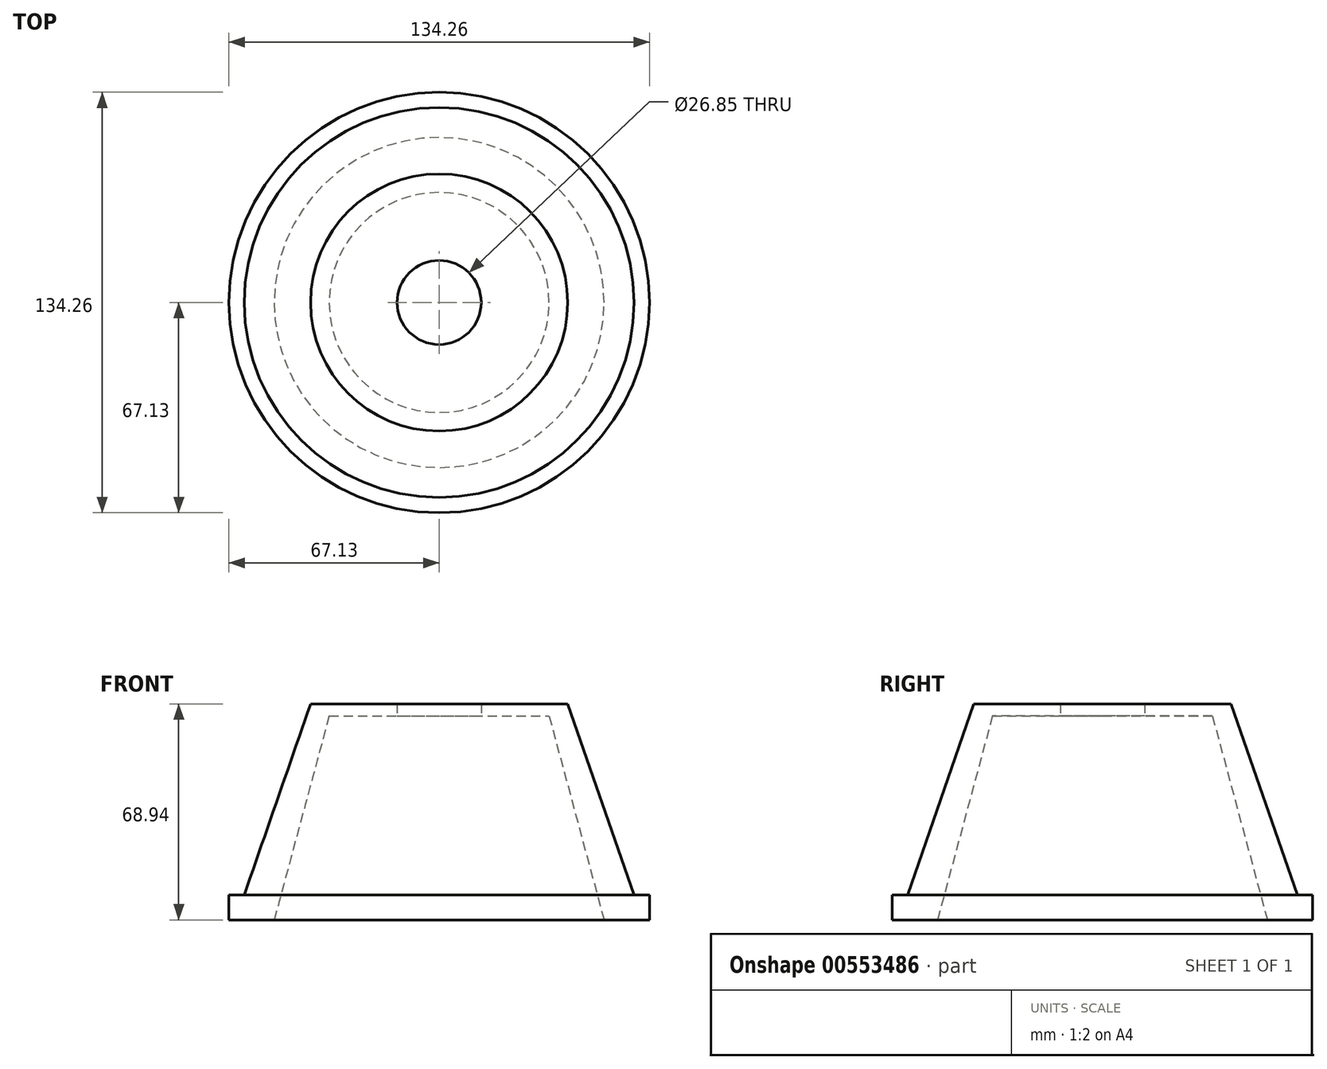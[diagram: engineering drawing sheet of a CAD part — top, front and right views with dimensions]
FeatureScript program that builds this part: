
annotation { "Feature Type Name" : "Feature", "Feature Type Description" : "" }
export const myFeature = defineFeature(function(context is Context, id is Id, definition is map)
    precondition{}
    {
        {
            var Q0;
            Q0=qCreatedBy(makeId("Front.planeOp"),FACE);
            var sketch = newSketch(context, id + "F0", { "sketchPlane" : qUnion([Q0])});
            skLineSegment(sketch, "E0", {"start": v(52.67, 0) * mm, "end": v(67.13, 0) * mm});
            skLineSegment(sketch, "E1", {"start": v(67.13, 0) * mm, "end": v(67.13, 8) * mm});
            skLineSegment(sketch, "E2", {"start": v(67.13, 8) * mm, "end": v(62.23, 8) * mm});
            skLineSegment(sketch, "E3", {"start": v(62.23, 8) * mm, "end": v(41.05, 68.94) * mm});
            skLineSegment(sketch, "E4", {"start": v(41.05, 68.94) * mm, "end": v(13.43, 68.94) * mm});
            skLineSegment(sketch, "E5", {"start": v(0, 0) * mm, "end": v(0, 44.4) * mm});
            skLineSegment(sketch, "E6", {"start": v(13.43, 68.94) * mm, "end": v(13.43, 65.07) * mm});
            skLineSegment(sketch, "E7", {"start": v(13.43, 65.07) * mm, "end": v(35.11, 65.07) * mm});
            skLineSegment(sketch, "E8", {"start": v(35.11, 65.07) * mm, "end": v(52.67, 0) * mm});
            skLineSegment(sketch, "E9", {"start": v(52.67, 0) * mm, "end": v(56.29, 0) * mm});
            skSolve(sketch);
        }
        {
            var Q0;
            Q0=makeQuery(id+"F0.imprint","IMPRINT",FACE,{"disambiguationData":[TD([[makeQuery(id+"F0.imprint","IMPRINT",EDGE,{"derivedFrom":sQuery(id+"F0.wireOp",EDGE,"E0")}),1.0]])]});
            var Q1;
            Q1=sQuery(id+"F0.wireOp",EDGE,"E5");
            revolve(context, id + "F1", {"entities" : qUnion([Q0]), "axis" : qUnion([Q1]), "revolveType" : RevolveType.FULL});
        }
    });
